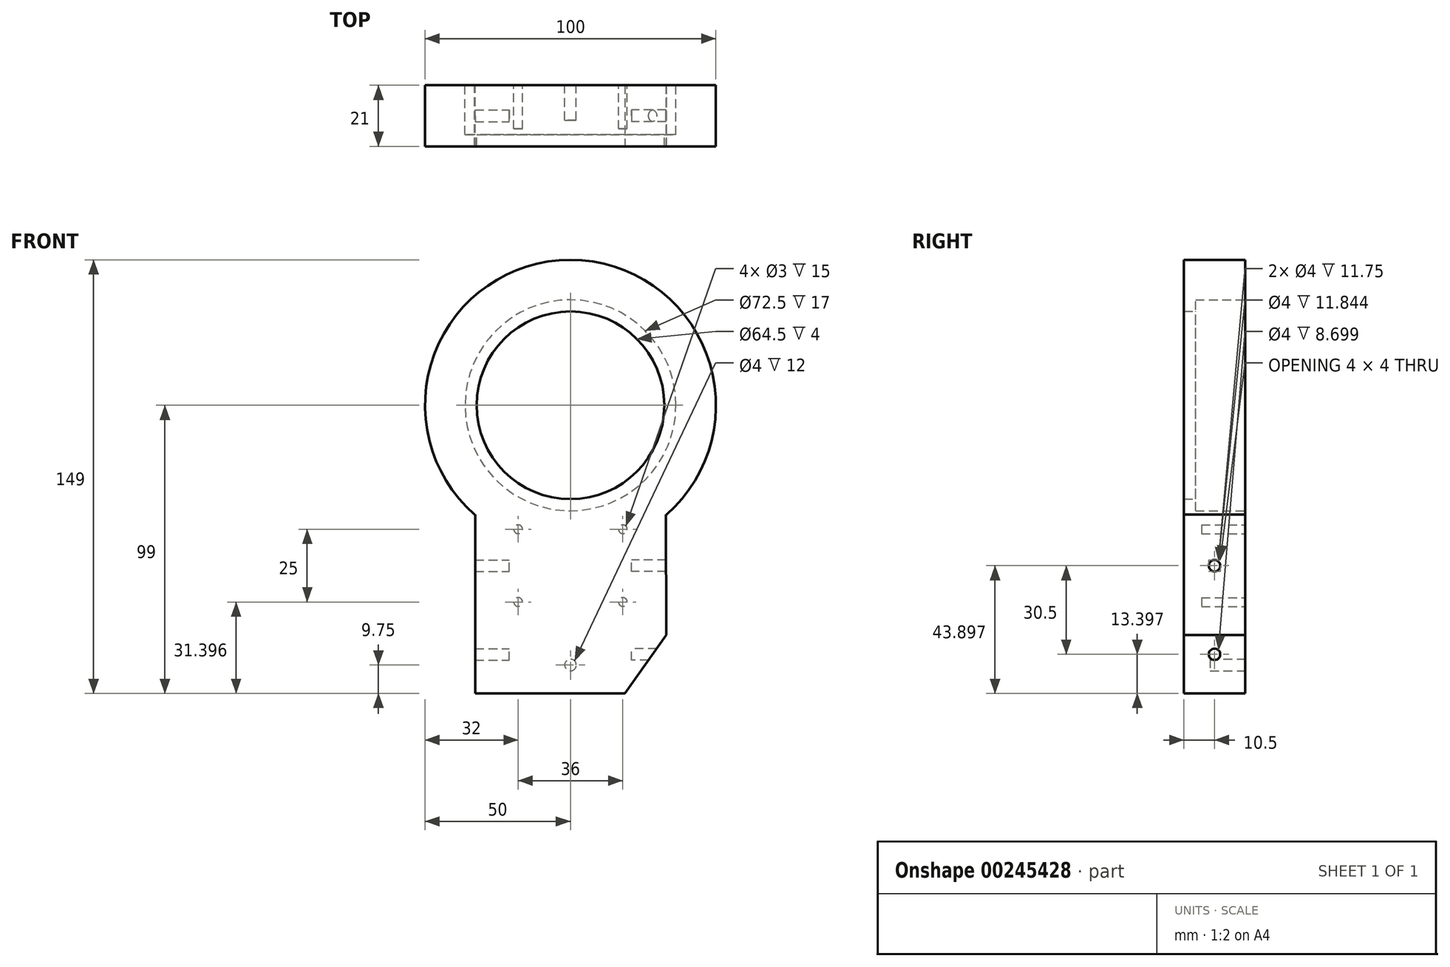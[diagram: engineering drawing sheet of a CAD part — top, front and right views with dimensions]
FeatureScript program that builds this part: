
annotation { "Feature Type Name" : "Feature", "Feature Type Description" : "" }
export const myFeature = defineFeature(function(context is Context, id is Id, definition is map)
    precondition{}
    {
        {
            var Q0;
            Q0=qCreatedBy(makeId("Front.planeOp"),FACE);
            var sketch = newSketch(context, id + "F0", { "sketchPlane" : qUnion([Q0])});
            skCircle(sketch, "E0", {"center": v(0, 0) * mm, "radius": 36.25 * mm});
            skArc(sketch, "E1", {"start": v(50, 0) * mm, "mid": v(0, 50) * mm, "end": v(-50, 0) * mm});
            skPoint(sketch, "E2.endSnap0", {"position": v(0, -99) * mm});
            skLineSegment(sketch, "E3.trimOffspring", {"start": v(-19, -99) * mm, "end": v(19, -99) * mm});
            skArc(sketch, "E4.MirrorCS", {"start": v(50, 0) * mm, "mid": v(45.55, -20.62) * mm, "end": v(33, -37.56) * mm});
            skLineSegment(sketch, "E5.trimOffspring", {"start": v(33, -37.56) * mm, "end": v(33, -79) * mm});
            skLineSegment(sketch, "E6.trimOffspring", {"start": v(-33, -37.56) * mm, "end": v(-33, -79) * mm});
            skArc(sketch, "E7.trimOffspring", {"start": v(-33, -37.56) * mm, "mid": v(-45.55, -20.62) * mm, "end": v(-50, 0) * mm});
            skLineSegment(sketch, "E8", {"start": v(0, -99) * mm, "end": v(0, -81.4) * mm});
            skLineSegment(sketch, "E9.MirrorCS", {"start": v(33, -79) * mm, "end": v(19, -99) * mm});
            skLineSegment(sketch, "E10", {"start": v(-19, -99) * mm, "end": v(-33, -99) * mm});
            skLineSegment(sketch, "E11", {"start": v(-33, -99) * mm, "end": v(-33, -79) * mm});
            skSolve(sketch);
        }
        {
            var Q0;
            Q0=qSketchRegion(id+"F0",true);
            extrude(context, id + "F1", {"entities" : qUnion([Q0]), "depth" : 17 * mm});
        }
        {
            var Q0;
            Q0=makeQuery(id+"F1.opExtrude","CAP_FACE",FACE,{"disambiguationData":[OSD([sQuery(id+"F0.wireOp",EDGE,"E0"),sQuery(id+"F0.wireOp",EDGE,"E1"),sQuery(id+"F0.wireOp",EDGE,"9Qu72541-LivO-jTMm-oUwD-ZALQE2Hvik1n"),sQuery(id+"F0.wireOp",EDGE,"i4TymV6R-teZx-C7h1-2yMt-q0MvK4pHcOex"),sQuery(id+"F0.wireOp",EDGE,"pD05HJNU-Muf5-boTQ-xGwQ-RlADy1BkldT5")])],"isStart":false});
            var sketch = newSketch(context, id + "F2", { "sketchPlane" : qUnion([Q0])});
            skCircle(sketch, "E12", {"center": v(0, 0) * mm, "radius": 32.25 * mm});
            skLineSegment(sketch, "E13.left", {"start": v(33, -37.56) * mm, "end": v(33, -79) * mm});
            skLineSegment(sketch, "E13.right", {"start": v(-33, -37.56) * mm, "end": v(-33, -37.56) * mm});
            skLineSegment(sketch, "E14", {"start": v(-33, -37.56) * mm, "end": v(-33, -99) * mm});
            skLineSegment(sketch, "E15", {"start": v(33, -79) * mm, "end": v(19, -99) * mm});
            skLineSegment(sketch, "E16", {"start": v(-33, -99) * mm, "end": v(19, -99) * mm});
            skArc(sketch, "E17", {"start": v(33, -37.56) * mm, "mid": v(0, 50) * mm, "end": v(-33, -37.56) * mm});
            skSolve(sketch);
        }
        {
            var Q0;
            Q0=qSketchRegion(id+"F2",true);
            extrude(context, id + "F3", {"entities" : qUnion([Q0]), "operationType" : NewBodyOperationType.ADD, "depth" : 4 * mm});
        }
        {
            var Q0;
            Q0=makeQuery(id+"F1.opExtrude","CAP_FACE",FACE,{"disambiguationData":[OSD([sQuery(id+"F0.wireOp",EDGE,"E0"),sQuery(id+"F0.wireOp",EDGE,"E1"),sQuery(id+"F0.wireOp",EDGE,"9Qu72541-LivO-jTMm-oUwD-ZALQE2Hvik1n"),sQuery(id+"F0.wireOp",EDGE,"i4TymV6R-teZx-C7h1-2yMt-q0MvK4pHcOex"),sQuery(id+"F0.wireOp",EDGE,"pD05HJNU-Muf5-boTQ-xGwQ-RlADy1BkldT5")])],"isStart":true});
            var sketch = newSketch(context, id + "F4", { "sketchPlane" : qUnion([Q0])});
            skCircle(sketch, "E18", {"center": v(-18, -42.6) * mm, "radius": 1.5 * mm});
            skCircle(sketch, "E19", {"center": v(18, -42.6) * mm, "radius": 1.5 * mm});
            skCircle(sketch, "E20", {"center": v(18, -67.6) * mm, "radius": 1.5 * mm});
            skCircle(sketch, "E21", {"center": v(-18, -67.6) * mm, "radius": 1.5 * mm});
            skSolve(sketch);
        }
        {
            var Q0;
            Q0=qSketchRegion(id+"F4",true);
            extrude(context, id + "F5", {"entities" : qUnion([Q0]), "operationType" : NewBodyOperationType.REMOVE, "oppositeDirection" : true, "depth" : 15 * mm});
        }
        {
            var Q0;
            Q0=qCreatedBy(makeId("Right.planeOp"),FACE);
            cPlane(context, id + "F6", {"entities" : qUnion([Q0]), "cplaneType" : CPlaneType.OFFSET, "offset" : (33 - 12) * mm, "width" : 150 * mm, "height" : 150 * mm});
        }
        {
            var Q0;
            Q0=qCreatedBy(id+"F6.planeOp",FACE);
            var sketch = newSketch(context, id + "F7", { "sketchPlane" : qUnion([Q0])});
            skLineSegment(sketch, "E22", {"start": v(0, 0) * mm, "end": v(0, -42.6) * mm});
            skLineSegment(sketch, "E23", {"start": v(0, -42.6) * mm, "end": v(0, -67.6) * mm});
            skLineSegment(sketch, "E24", {"start": v(0, -67.6) * mm, "end": v(0, -85.6) * mm});
            skLineSegment(sketch, "E25", {"start": v(0, -55.1) * mm, "end": v(-21, -55.1) * mm});
            skLineSegment(sketch, "E26", {"start": v(0, -85.6) * mm, "end": v(-21, -85.6) * mm});
            skCircle(sketch, "E27", {"center": v(-10.5, -55.1) * mm, "radius": 2 * mm});
            skCircle(sketch, "E28", {"center": v(-10.5, -85.6) * mm, "radius": 2 * mm});
            skSolve(sketch);
        }
        {
            var Q0;
            Q0=qSketchRegion(id+"F7",true);
            extrude(context, id + "F8", {"entities" : qUnion([Q0]), "operationType" : NewBodyOperationType.REMOVE, "depth" : 25 * mm});
        }
        {
            var Q0;
            Q0=qCreatedBy(makeId("Right.planeOp"),FACE);
            cPlane(context, id + "F9", {"entities" : qUnion([Q0]), "cplaneType" : CPlaneType.OFFSET, "offset" : (33 - 12) * mm, "oppositeDirection" : true, "width" : 150 * mm, "height" : 150 * mm});
        }
        {
            var Q0;
            Q0=qCreatedBy(id+"F9.planeOp",FACE);
            var sketch = newSketch(context, id + "F10", { "sketchPlane" : qUnion([Q0])});
            skLineSegment(sketch, "E29", {"start": v(0, 0) * mm, "end": v(0, -42.6) * mm});
            skLineSegment(sketch, "E30", {"start": v(0, -42.6) * mm, "end": v(0, -67.6) * mm});
            skLineSegment(sketch, "E31", {"start": v(0, -67.6) * mm, "end": v(0, -85.6) * mm});
            skLineSegment(sketch, "E32", {"start": v(0, -85.6) * mm, "end": v(-21, -85.6) * mm});
            skLineSegment(sketch, "E33", {"start": v(0, -55.1) * mm, "end": v(-21, -55.1) * mm});
            skCircle(sketch, "E34", {"center": v(-10.5, -55.1) * mm, "radius": 2 * mm});
            skCircle(sketch, "E35", {"center": v(-10.5, -85.6) * mm, "radius": 2 * mm});
            skSolve(sketch);
        }
        {
            var Q0;
            Q0=qSketchRegion(id+"F10",true);
            extrude(context, id + "F11", {"entities" : qUnion([Q0]), "operationType" : NewBodyOperationType.REMOVE, "oppositeDirection" : true, "depth" : 25 * mm});
        }
        {
            var Q0;
            Q0=makeQuery(id+"F1.opExtrude","CAP_FACE",FACE,{"disambiguationData":[OSD([sQuery(id+"F0.wireOp",EDGE,"E0"),sQuery(id+"F0.wireOp",EDGE,"E1"),sQuery(id+"F0.wireOp",EDGE,"E3.trimOffspring"),sQuery(id+"F0.wireOp",EDGE,"E4.MirrorCS"),sQuery(id+"F0.wireOp",EDGE,"E5.trimOffspring"),sQuery(id+"F0.wireOp",EDGE,"E6.trimOffspring"),sQuery(id+"F0.wireOp",EDGE,"E7.trimOffspring"),sQuery(id+"F0.wireOp",EDGE,"E9.MirrorCS"),sQuery(id+"F0.wireOp",EDGE,"E10"),sQuery(id+"F0.wireOp",EDGE,"E11")])],"isStart":true});
            var sketch = newSketch(context, id + "F12", { "sketchPlane" : qUnion([Q0])});
            skLineSegment(sketch, "E36", {"start": v(0, -99) * mm, "end": v(0, -79.5) * mm});
            skCircle(sketch, "E37", {"center": v(0, -89.25) * mm, "radius": 2 * mm});
            skSolve(sketch);
        }
        {
            var Q0;
            Q0=qSketchRegion(id+"F12",true);
            extrude(context, id + "F13", {"entities" : qUnion([Q0]), "operationType" : NewBodyOperationType.REMOVE, "oppositeDirection" : true, "depth" : 12 * mm});
        }
        {
            var Q0;
            Q0=makeQuery(id+"F3.opExtrude","CAP_FACE",FACE,{"disambiguationData":[OSD([sQuery(id+"F2.wireOp",EDGE,"E12"),sQuery(id+"F2.wireOp",EDGE,"E13.left"),sQuery(id+"F2.wireOp",EDGE,"E14"),sQuery(id+"F2.wireOp",EDGE,"E15"),sQuery(id+"F2.wireOp",EDGE,"E16"),sQuery(id+"F2.wireOp",EDGE,"E17")])],"isStart":false});
            var sketch = newSketch(context, id + "F14", { "sketchPlane" : qUnion([Q0])});
            skLineSegment(sketch, "E38", {"start": v(33, -37.56) * mm, "end": v(32.75, -37.56) * mm});
            skLineSegment(sketch, "E39", {"start": v(32.75, -37.56) * mm, "end": v(32.95, -79) * mm});
            skLineSegment(sketch, "E40", {"start": v(19, -99) * mm, "end": v(18.75, -99) * mm});
            skLineSegment(sketch, "E41", {"start": v(18.75, -99) * mm, "end": v(32.95, -79) * mm});
            skPoint(sketch, "E42.orphan", {"position": v(33, -89.84) * mm});
            skLineSegment(sketch, "E43", {"start": v(-33, -37.56) * mm, "end": v(-32.75, -37.56) * mm});
            skLineSegment(sketch, "E44", {"start": v(-32.75, -37.56) * mm, "end": v(-32.75, -103.9) * mm});
            skLineSegment(sketch, "E45", {"start": v(-32.75, -103.9) * mm, "end": v(18.75, -99) * mm});
            skLineSegment(sketch, "E46", {"start": v(-33, -37.56) * mm, "end": v(-37.55, -48.77) * mm});
            skLineSegment(sketch, "E47", {"start": v(-37.55, -48.77) * mm, "end": v(-37.55, -109.62) * mm});
            skLineSegment(sketch, "E48", {"start": v(-37.55, -109.62) * mm, "end": v(30.63, -103.31) * mm});
            skLineSegment(sketch, "E49", {"start": v(30.63, -103.31) * mm, "end": v(39, -80.77) * mm});
            skLineSegment(sketch, "E50", {"start": v(39, -80.77) * mm, "end": v(39, -37.56) * mm});
            skLineSegment(sketch, "E51", {"start": v(39, -37.56) * mm, "end": v(33, -37.56) * mm});
            skSolve(sketch);
        }
        {
            var Q0;
            Q0=qSketchRegion(id+"F14",true);
            extrude(context, id + "F15", {"entities" : qUnion([Q0]), "operationType" : NewBodyOperationType.REMOVE, "oppositeDirection" : true, "depth" : 25 * mm});
        }
    });
